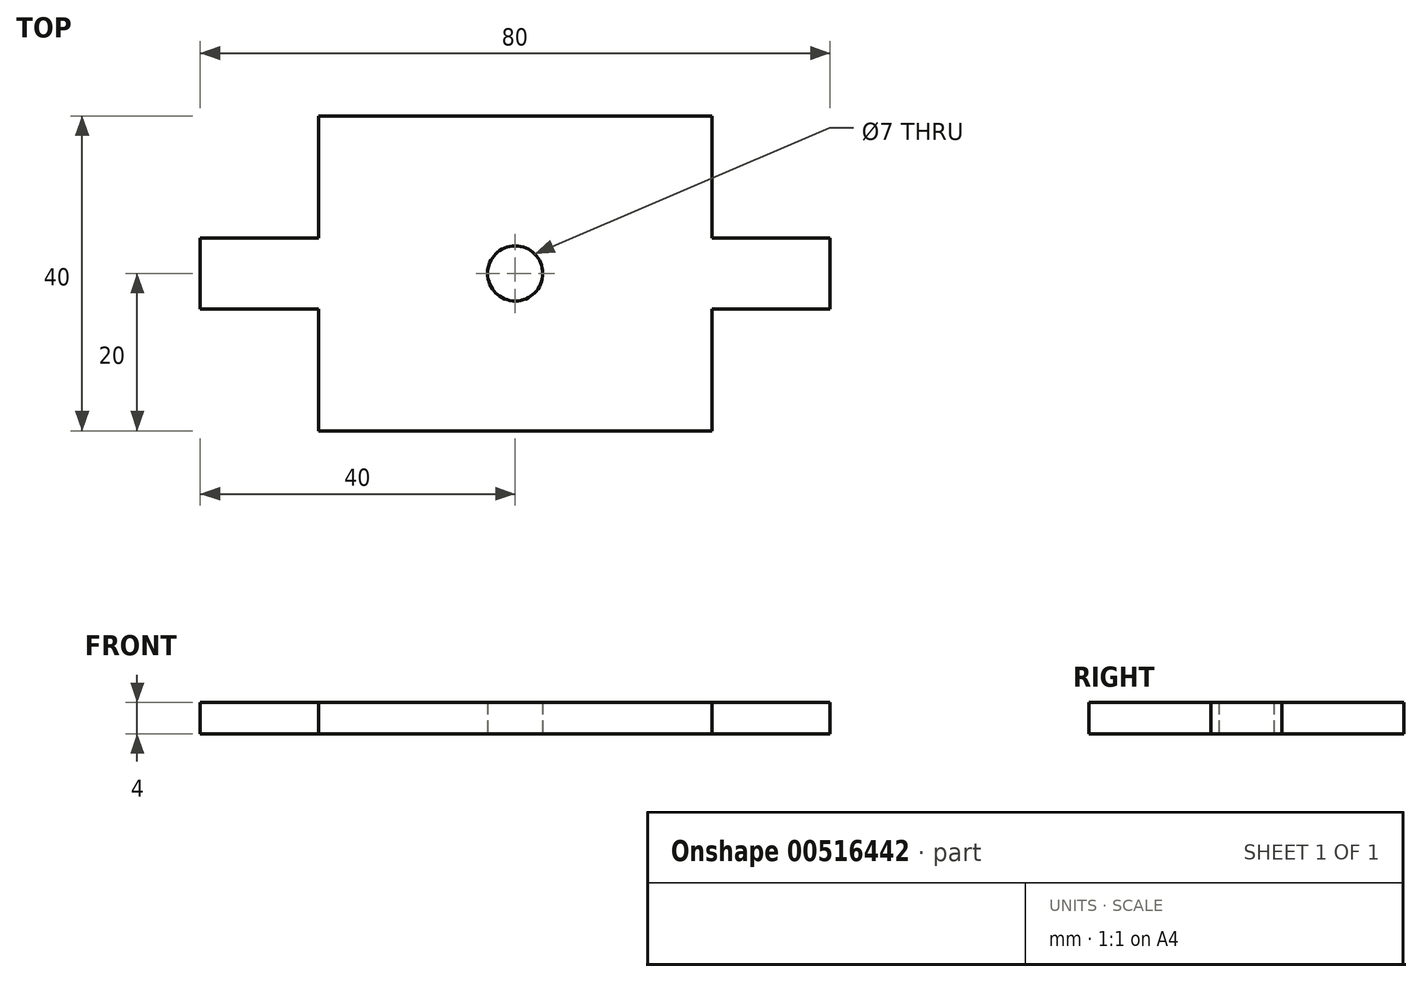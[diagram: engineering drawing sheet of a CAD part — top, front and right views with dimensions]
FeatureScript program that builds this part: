
annotation { "Feature Type Name" : "Feature", "Feature Type Description" : "" }
export const myFeature = defineFeature(function(context is Context, id is Id, definition is map)
    precondition{}
    {
        {
            var Q0;
            Q0=qCreatedBy(makeId("Top.planeOp"),FACE);
            var sketch = newSketch(context, id + "F0", { "sketchPlane" : qUnion([Q0])});
            skLineSegment(sketch, "E0.bottom", {"start": v(25, -20) * mm, "end": v(-25, -20) * mm});
            skLineSegment(sketch, "E0.top", {"start": v(25, 20) * mm, "end": v(-25, 20) * mm});
            skLineSegment(sketch, "E0.left", {"start": v(40, -4.5) * mm, "end": v(40, 4.5) * mm});
            skPoint(sketch, "E0.middle", {"position": v(0, 0) * mm});
            skLineSegment(sketch, "E1.top", {"start": v(-40, 4.5) * mm, "end": v(-25, 4.5) * mm});
            skLineSegment(sketch, "E1.right", {"start": v(-25, 20) * mm, "end": v(-25, 4.5) * mm});
            skLineSegment(sketch, "E2.top", {"start": v(-40, -4.5) * mm, "end": v(-25, -4.5) * mm});
            skLineSegment(sketch, "E2.right", {"start": v(-25, -20) * mm, "end": v(-25, -4.5) * mm});
            skLineSegment(sketch, "E3.top", {"start": v(40, 4.5) * mm, "end": v(25, 4.5) * mm});
            skLineSegment(sketch, "E3.right", {"start": v(25, 20) * mm, "end": v(25, 4.5) * mm});
            skLineSegment(sketch, "E4.top", {"start": v(40, -4.5) * mm, "end": v(25, -4.5) * mm});
            skLineSegment(sketch, "E4.right", {"start": v(25, -20) * mm, "end": v(25, -4.5) * mm});
            skCircle(sketch, "E5", {"center": v(0, 0) * mm, "radius": 3.5 * mm});
            skPoint(sketch, "E6.orphan", {"position": v(-40, 20) * mm});
            skPoint(sketch, "E7.orphan", {"position": v(-40, -20) * mm});
            skPoint(sketch, "E8.orphan", {"position": v(40, -20) * mm});
            skPoint(sketch, "E9.orphan", {"position": v(40, 20) * mm});
            skLineSegment(sketch, "E10", {"start": v(-40, 4.5) * mm, "end": v(-40, -4.5) * mm});
            skSolve(sketch);
        }
        {
            var Q0;
            Q0 = qSketchRegion(id + "F0", true);
            extrude(context, id + "F1", {"entities" : qUnion([Q0]), "depth" : 4 * mm, "offsetDistance" : 25 * mm});
        }
    });
